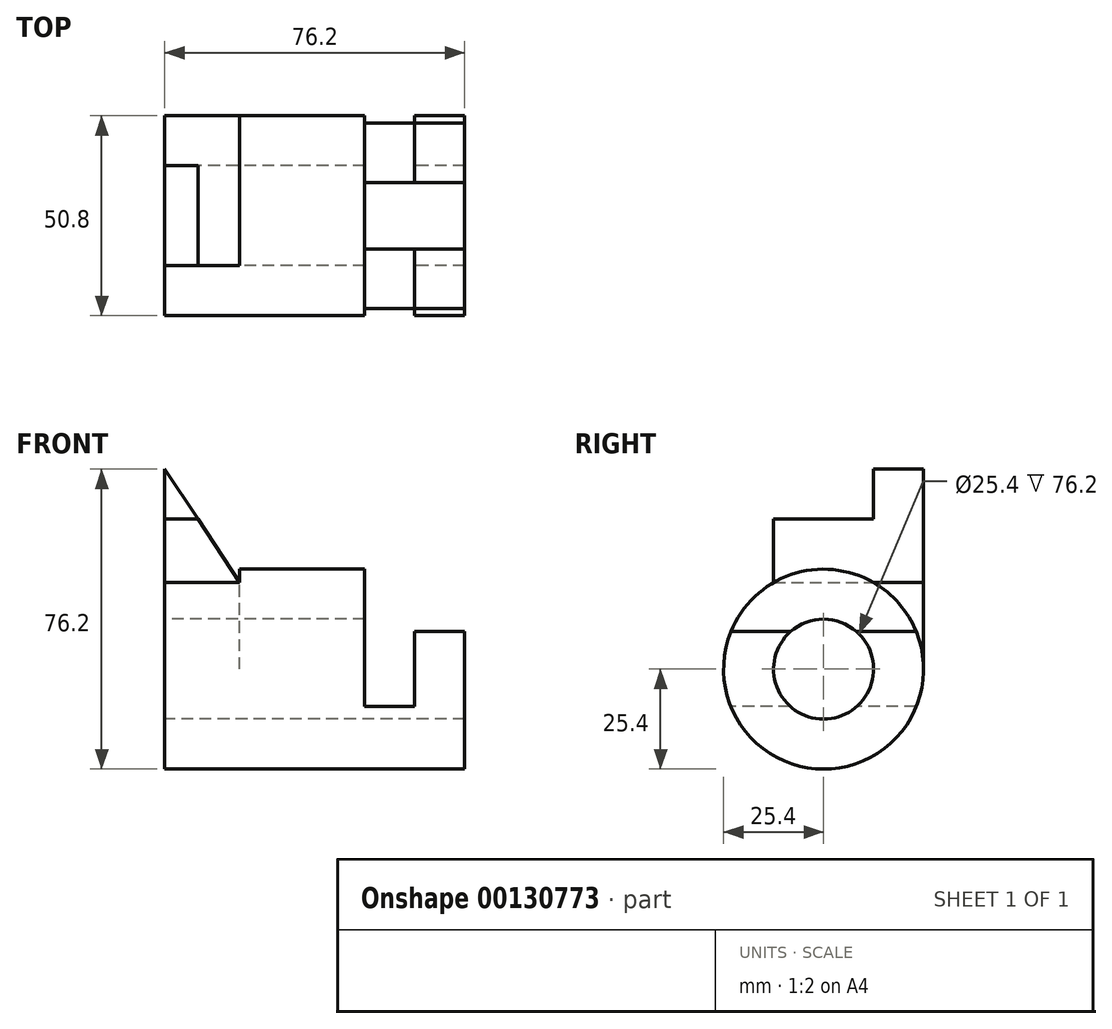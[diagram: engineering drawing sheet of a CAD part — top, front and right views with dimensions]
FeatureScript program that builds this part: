
annotation { "Feature Type Name" : "Feature", "Feature Type Description" : "" }
export const myFeature = defineFeature(function(context is Context, id is Id, definition is map)
    precondition{}
    {
        {
            var Q0;
            Q0=qCreatedBy(makeId("Right.planeOp"),FACE);
            var sketch = newSketch(context, id + "F0", { "sketchPlane" : qUnion([Q0])});
            skCircle(sketch, "E0", {"center": v(0, 0) * mm, "radius": 25.4 * mm});
            skCircle(sketch, "E1", {"center": v(0, 0) * mm, "radius": 12.7 * mm});
            skSolve(sketch);
        }
        {
            var Q0;
            Q0 = qSketchRegion(id + "F0", true);
            extrude(context, id + "F1", {"entities" : qUnion([Q0]), "depth" : 76.2 * mm});
        }
        {
            var Q0;
            Q0=qCreatedBy(makeId("Front.planeOp"),FACE);
            var sketch = newSketch(context, id + "F2", { "sketchPlane" : qUnion([Q0])});
            skLineSegment(sketch, "E2", {"start": v(0, 25.4) * mm, "end": v(76.2, 25.4) * mm});
            skLineSegment(sketch, "E3", {"start": v(50.8, 25.4) * mm, "end": v(50.8, -9.53) * mm});
            skLineSegment(sketch, "E4", {"start": v(50.8, -9.53) * mm, "end": v(63.5, -9.53) * mm});
            skLineSegment(sketch, "E5", {"start": v(63.5, -9.52) * mm, "end": v(63.5, 9.53) * mm});
            skLineSegment(sketch, "E6", {"start": v(63.5, 9.53) * mm, "end": v(76.2, 9.53) * mm});
            skLineSegment(sketch, "E7", {"start": v(76.2, 9.53) * mm, "end": v(76.2, 25.4) * mm});
            skLineSegment(sketch, "E8", {"start": v(76.2, 25.4) * mm, "end": v(50.8, 25.4) * mm});
            skSolve(sketch);
        }
        {
            var Q0;
            Q0 = qSketchRegion(id + "F2", true);
            extrude(context, id + "F3", {"entities" : qUnion([Q0]), "operationType" : NewBodyOperationType.REMOVE, "oppositeDirection" : true, "depth" : 25.4 * mm, "hasSecondDirection" : true, "secondDirectionOppositeDirection" : false, "secondDirectionDepth" : 25.4 * mm});
        }
        {
            var Q0;
            Q0=qCreatedBy(makeId("Right.planeOp"),FACE);
            var sketch = newSketch(context, id + "F4", { "sketchPlane" : qUnion([Q0])});
            skLineSegment(sketch, "E9", {"start": v(-12.7, 0) * mm, "end": v(25.4, 0) * mm});
            skLineSegment(sketch, "E10", {"start": v(25.4, 0) * mm, "end": v(25.4, 50.8) * mm});
            skLineSegment(sketch, "E11", {"start": v(25.4, 50.8) * mm, "end": v(-12.7, 50.8) * mm});
            skLineSegment(sketch, "E12", {"start": v(-12.7, 50.8) * mm, "end": v(-12.7, 0) * mm});
            skCircle(sketch, "E13.0", {"center": v(0, 0) * mm, "radius": 12.7 * mm});
            skSolve(sketch);
        }
        {
            var Q0;
            {var subQ1=sQuery(id+"F4.wireOp",EDGE,"E10");Q0=makeQuery(id+"F4.imprint","IMPRINT",FACE,{"disambiguationData":[TD([[makeQuery(id+"F4.imprint","IMPRINT",EDGE,{"derivedFrom":subQ1}),1.0]])]});}
            extrude(context, id + "F5", {"entities" : qUnion([Q0]), "operationType" : NewBodyOperationType.ADD, "depth" : 19.05 * mm});
        }
        {
            var Q0;
            Q0=qCreatedBy(makeId("Right.planeOp"),FACE);
            var sketch = newSketch(context, id + "F6", { "sketchPlane" : qUnion([Q0])});
            skPoint(sketch, "E14.0", {"position": v(-12.7, 50.8) * mm});
            skLineSegment(sketch, "E15.bottom", {"start": v(-12.7, 50.8) * mm, "end": v(12.7, 50.8) * mm});
            skLineSegment(sketch, "E15.top", {"start": v(-12.7, 38.1) * mm, "end": v(12.7, 38.1) * mm});
            skLineSegment(sketch, "E15.left", {"start": v(-12.7, 50.8) * mm, "end": v(-12.7, 38.1) * mm});
            skLineSegment(sketch, "E15.right", {"start": v(12.7, 50.8) * mm, "end": v(12.7, 38.1) * mm});
            skSolve(sketch);
        }
        {
            var Q0;
            Q0 = qSketchRegion(id + "F6", true);
            extrude(context, id + "F7", {"entities" : qUnion([Q0]), "operationType" : NewBodyOperationType.REMOVE, "depth" : 25.4 * mm});
        }
        {
            var Q0;
            Q0=qCreatedBy(makeId("Front.planeOp"),FACE);
            var sketch = newSketch(context, id + "F8", { "sketchPlane" : qUnion([Q0])});
            skPoint(sketch, "E16.0", {"position": v(0, 50.8) * mm});
            skPoint(sketch, "E17.0", {"position": v(19.05, 22) * mm});
            skLineSegment(sketch, "E18", {"start": v(0, 50.8) * mm, "end": v(19.05, 22) * mm});
            skLineSegment(sketch, "E19", {"start": v(19.05, 50.8) * mm, "end": v(0, 50.8) * mm});
            skLineSegment(sketch, "E20", {"start": v(19.05, 50.8) * mm, "end": v(19.05, 22) * mm});
            skSolve(sketch);
        }
        {
            var Q0;
            Q0 = qSketchRegion(id + "F8", true);
            extrude(context, id + "F9", {"entities" : qUnion([Q0]), "operationType" : NewBodyOperationType.REMOVE, "endBound" : BoundingType.THROUGH_ALL, "depth" : 25.4 * mm, "hasSecondDirection" : true, "secondDirectionOppositeDirection" : true, "secondDirectionDepth" : 25.4 * mm});
        }
    });
